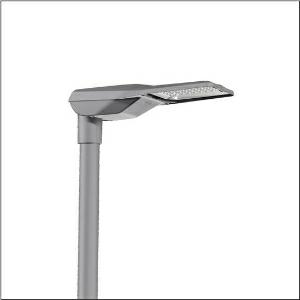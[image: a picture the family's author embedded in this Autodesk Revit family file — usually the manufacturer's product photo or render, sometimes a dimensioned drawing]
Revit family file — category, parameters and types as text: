
# Revit family: streetlight_sl_21_iq_mini___stw1_0a_5xe2e61d08hb_c7c8
name_source: partatom
category: Lighting Fixtures
units: mm (PartAtom-declared; Revit-internal decimal feet)

## family parameters
Cut with Voids When Loaded = No
Host = Face
Light Source = No
Part Type = Normal
Room Calculation Point = No
Round Connector Dimension = Use Diameter
Shared = No

## types (1)
- --- (1 x LED, 8480 lm, 70.9 W, 2700K)
    Apparent Load = 71 VA
    CIE Flux Codes = 38 75 98 100 100
    Color Rendering = 70
    Color Temperature = 2700K
    Default Elevation = 1800 mm
    Description = Streetlight SL 21 iQ mini, mast luminaire, primary light control with lens, of PMMA, primary optical cover: cover, of toughened safety glass, transparent, light distribution: STW1.0a, light emission: direct distribution, primary light characteristic: asymmetric, installation type: post-top, side-entry, LED, High Power LED, rated luminous flux: 8.480lm, luminous efficacy: 120lm/W, light colour: 727, colour temperature: 2700K, control gear: iQ-Comfort, control: Auto-Match, Temp-Guard, Lumen-Switch, Night-Set, Smart-Wire, Light-Fading, Desk-Remote (wireless, voltage-free reading and setting of iQ features in the workshop via application-optimized NFC function/RFID function), optimised constant luminous flux control (CLO 2.0), pre-setting: linear dimming characteristic, mains connection: 220..240V, AC, 50/60Hz, start of lifetime: 71W, end of service life: 75W, reduction: 31W, luminaire housing, of diecast aluminium, powder-coated, SITECO metallic grey (DB 702S), corrosivity category C5 high according to DIN EN ISO 12944, please order mast flange separately, inclination adjustable: 0°, 5°, 10°, 15°, sealing non-destructively replaceable, multi-level sealing system, length: 628mm, width: 235mm, height: 110mm, mast flange for spigot size: 42mm (side-entry): 5XC10008XM4, 60/48mm (side-entry/post-top): 5XC10108XM2, 76/60mm (side-entry/post-top): 5XC10108XM1, mounting height: 4..8m, protection rating (complete): IP66, insulation class (complete): insulation class II (safety insulation), certification: CE, ENEC, ENEC+, VDE, impact resistance: IK10, permissible operating ambient temperature for outdoor applications: -40..+50°C, standard-compliant lighting for roads and squares, packaging unit: 1 piece

Light Distribution: STW1.0a
    Height = 110 mm
    Lamp = 1 x LED
    Lamp Light Flux = 8480 lm
    Lamp Power = 70.9 W
    Lamp count = 1
    Length = 625 mm
    Luminous efficacy = 120 lm/W
    Manufacturer = Siteco
    ModVariant = No
    Model = 5XE2E61D08HB
    Number of Poles = 1
    OnlyDefault = Yes
    Power Factor = 1
    Product Name = Streetlight SL 21 iQ mini | STW1.0a
    Product group = mast luminaire | pylon top
    ProductGroupID = 6100
    Protection Class = Protection class II
    Protection Degree = IP 66
    RLX_Detail_Level = 1
    RLX_Emergency_Light_Flux = 0 lm
    RLX_Emergency_Type = 0
    RLX_Emergency_Type_DB = No
    RlxData = <blob elided: 26317 chars, md5=723c3666>
    Socket = socket
    Standby Power = 0 W
    System Light Flux = 8480 lm
    System Power = 71 W
    Type Comments = factory setting: luminous flux: 100 % | dim-lin: 254 | 711 mA
    Type Image = l_1003519.jpg
    URL = http://relux.com
    VarID = @adj_157413
    Voltage = 0 V
    Weight = 0.00 kg
    Width = 234 mm

## geometry (parser evidence)
native form markers: Blend x4, Sweep x12
no freeform markers — native parametric forms only
